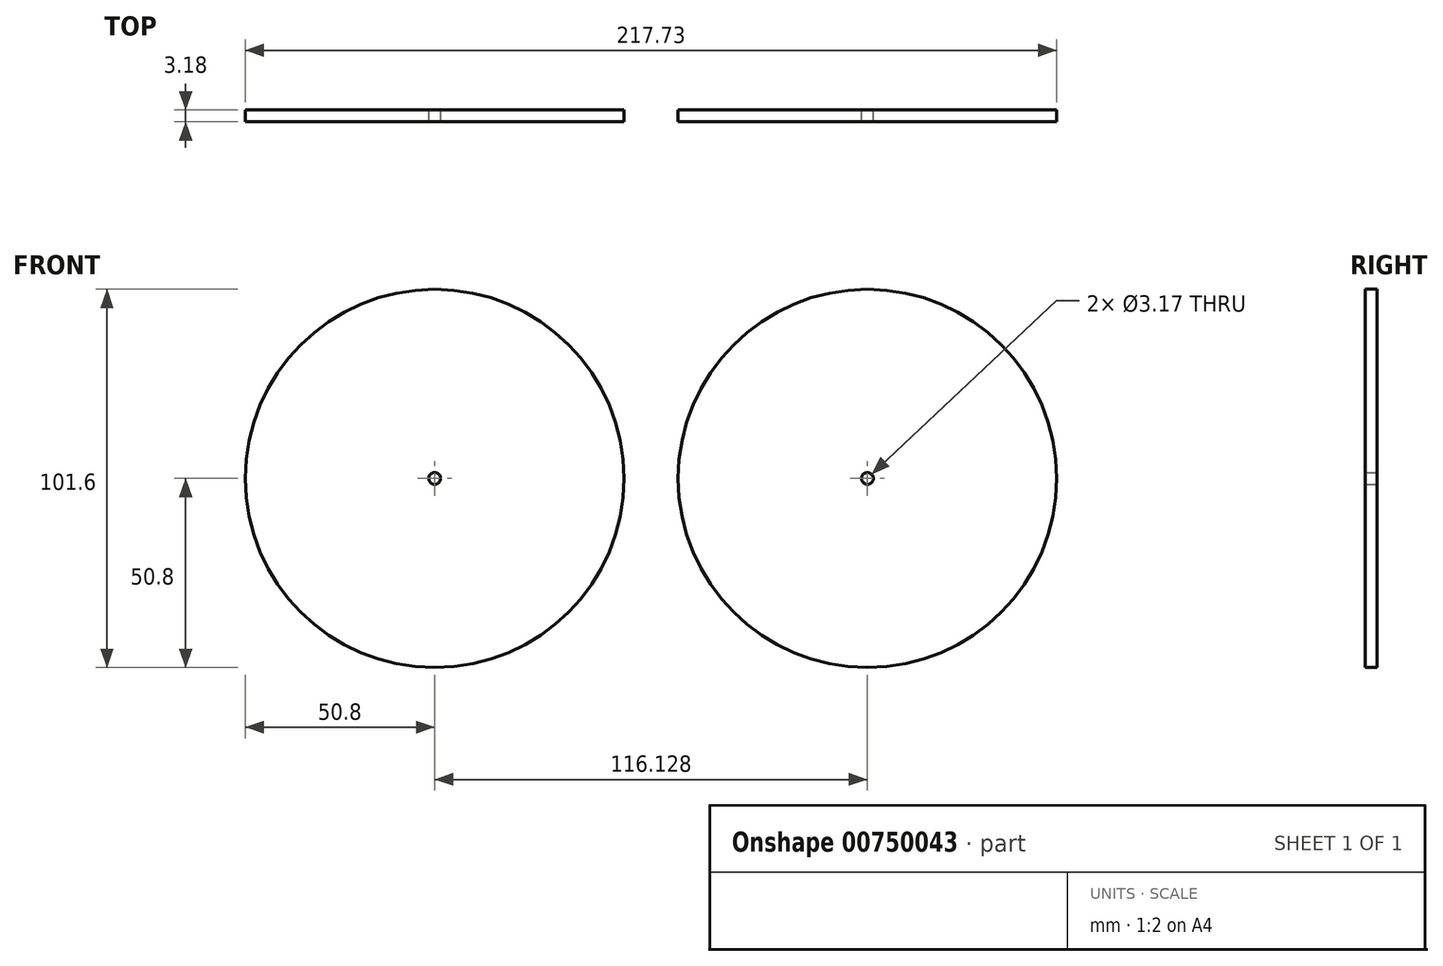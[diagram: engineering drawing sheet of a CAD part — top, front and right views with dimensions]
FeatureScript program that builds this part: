
annotation { "Feature Type Name" : "Feature", "Feature Type Description" : "" }
export const myFeature = defineFeature(function(context is Context, id is Id, definition is map)
    precondition{}
    {
        {
            var Q0;
            Q0=qCreatedBy(makeId("Front.planeOp"),FACE);
            var sketch = newSketch(context, id + "F0", { "sketchPlane" : qUnion([Q0])});
            skCircle(sketch, "E0", {"center": v(0, 0) * mm, "radius": 50.8 * mm});
            skCircle(sketch, "E1", {"center": v(0, 0) * mm, "radius": 1.59 * mm});
            skSolve(sketch);
        }
        {
            var Q0;
            Q0=makeQuery(id+"F0.imprint","IMPRINT",FACE,{"disambiguationData":[TD([[makeQuery(id+"F0.imprint","IMPRINT",EDGE,{"derivedFrom":sQuery(id+"F0.wireOp",EDGE,"E0")}),1.0]])]});
            extrude(context, id + "F1", {"entities" : qUnion([Q0]), "depth" : 3.17 * mm, "offsetDistance" : 25.4 * mm});
        }
        {
            var Q0;
            Q0=qCreatedBy(makeId("Front.planeOp"),FACE);
            var sketch = newSketch(context, id + "F2", { "sketchPlane" : qUnion([Q0])});
            skCircle(sketch, "E2", {"center": v(116.13, 0) * mm, "radius": 50.8 * mm});
            skCircle(sketch, "E3", {"center": v(116.13, 0) * mm, "radius": 1.59 * mm});
            skSolve(sketch);
        }
        {
            var Q0;
            Q0 = qSketchRegion(id + "F2", true);
            extrude(context, id + "F3", {"entities" : qUnion([Q0]), "depth" : 3.17 * mm, "offsetDistance" : 25.4 * mm});
        }
    });
